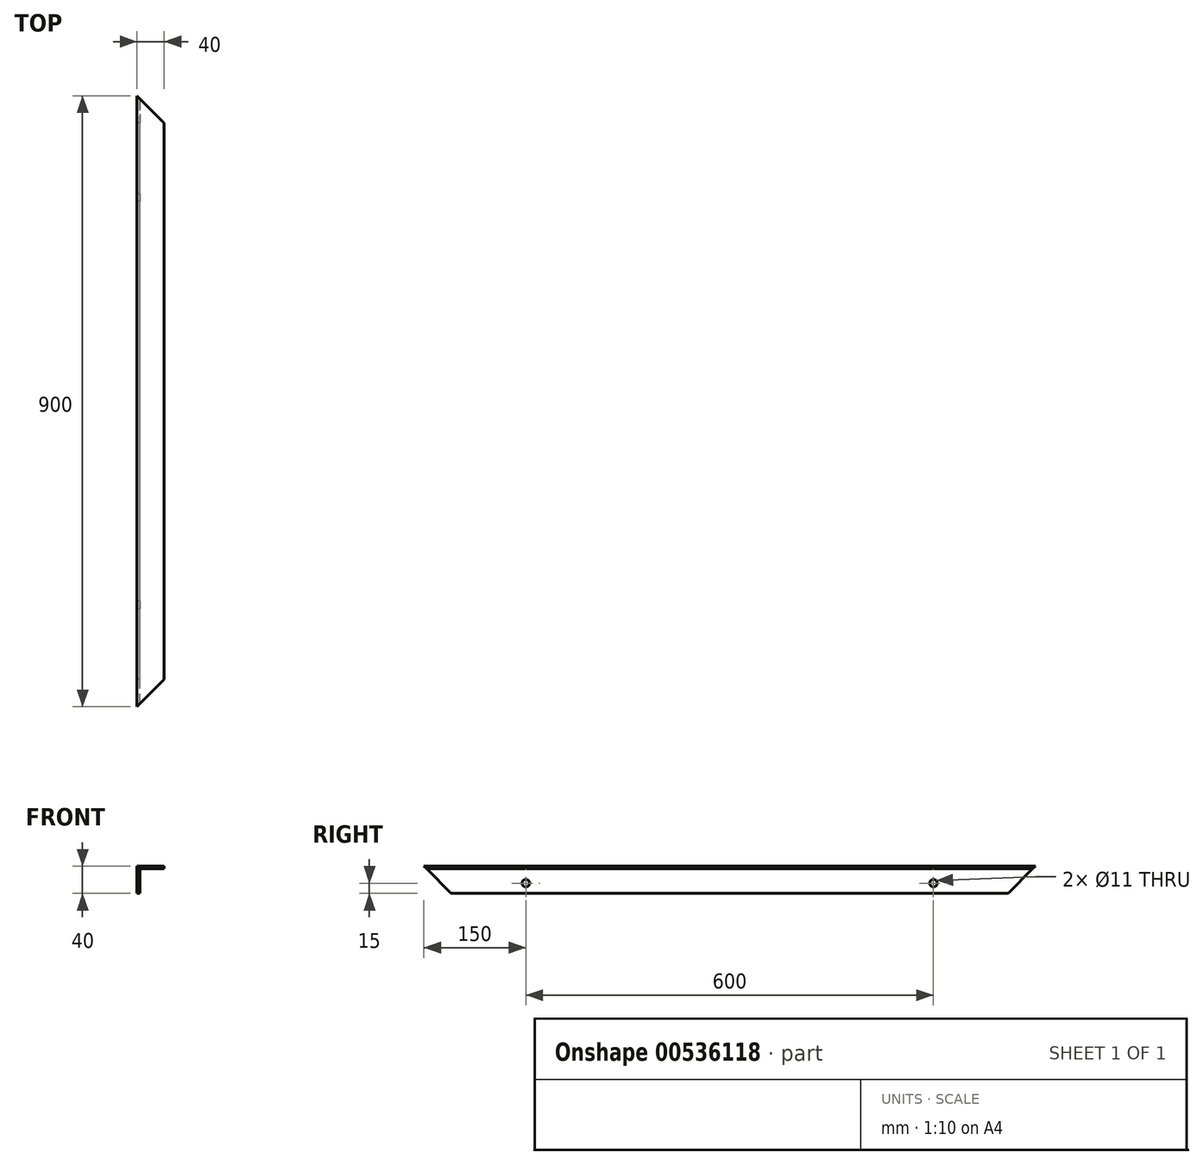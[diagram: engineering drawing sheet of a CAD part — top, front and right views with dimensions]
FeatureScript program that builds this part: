
annotation { "Feature Type Name" : "Feature", "Feature Type Description" : "" }
export const myFeature = defineFeature(function(context is Context, id is Id, definition is map)
    precondition{}
    {
        {
            var Q0;
            Q0=qCreatedBy(makeId("Front.planeOp"),FACE);
            var sketch = newSketch(context, id + "F0", { "sketchPlane" : qUnion([Q0])});
            skLineSegment(sketch, "E0", {"start": v(0, 0) * mm, "end": v(0, 40) * mm});
            skLineSegment(sketch, "E1", {"start": v(0, 40) * mm, "end": v(40, 40) * mm});
            skLineSegment(sketch, "E2.0", {"start": v(4, 36) * mm, "end": v(40, 36) * mm});
            skLineSegment(sketch, "E2.1", {"start": v(4, 0) * mm, "end": v(4, 36) * mm});
            skLineSegment(sketch, "E3", {"start": v(0, 0) * mm, "end": v(4, 0) * mm});
            skLineSegment(sketch, "E4", {"start": v(40, 36) * mm, "end": v(40, 40) * mm});
            skSolve(sketch);
        }
        {
            var Q0;
            Q0=makeQuery(id+"F0.imprint","IMPRINT",FACE,{"disambiguationData":[TD([[makeQuery(id+"F0.imprint","IMPRINT",EDGE,{"derivedFrom":sQuery(id+"F0.wireOp",EDGE,"E0")}),-1.0]])]});
            extrude(context, id + "F1", {"entities" : qUnion([Q0]), "endBound" : BoundingType.SYMMETRIC, "depth" : 900 * mm, "offsetDistance" : 25 * mm});
        }
        {
            var Q0;
            Q0=makeQuery(id+"F1.opExtrude","SWEPT_FACE",FACE,{"disambiguationData":[OSD([sQuery(id+"F0.wireOp",EDGE,"E0")])]});
            var sketch = newSketch(context, id + "F2", { "sketchPlane" : qUnion([Q0])});
            skLineSegment(sketch, "E5", {"start": v(-450, 40) * mm, "end": v(-410, 0) * mm});
            skLineSegment(sketch, "E6", {"start": v(450, 40) * mm, "end": v(410, 0) * mm});
            skSolve(sketch);
        }
        {
            var Q0;
            {var subQ0=sQuery(id+"F2.wireOp",EDGE,"E5");Q0=makeQuery(id+"F2.imprint","IMPRINT",FACE,{"disambiguationData":[TD([[makeQuery(id+"F2.imprint","IMPRINT",EDGE,{"derivedFrom":subQ0}),-1.0]])]});}
            var Q1;
            {var subQ0=sQuery(id+"F2.wireOp",EDGE,"E6");Q1=makeQuery(id+"F2.imprint","IMPRINT",FACE,{"disambiguationData":[TD([[makeQuery(id+"F2.imprint","IMPRINT",EDGE,{"derivedFrom":subQ0}),1.0]])]});}
            extrude(context, id + "F3", {"entities" : qUnion([Q0, Q1]), "operationType" : NewBodyOperationType.REMOVE, "oppositeDirection" : true, "depth" : 40 * mm, "offsetDistance" : 25 * mm});
        }
        {
            var Q0;
            Q0=makeQuery(id+"F1.opExtrude","SWEPT_FACE",FACE,{"disambiguationData":[OSD([sQuery(id+"F0.wireOp",EDGE,"E1")])]});
            var sketch = newSketch(context, id + "F4", { "sketchPlane" : qUnion([Q0])});
            skLineSegment(sketch, "E7", {"start": v(0, 450) * mm, "end": v(40, 410) * mm});
            skLineSegment(sketch, "E8", {"start": v(0, -450) * mm, "end": v(40, -410) * mm});
            skSolve(sketch);
        }
        {
            var Q0;
            {var subQ0=sQuery(id+"F4.wireOp",EDGE,"E7");Q0=makeQuery(id+"F4.imprint","IMPRINT",FACE,{"disambiguationData":[TD([[makeQuery(id+"F4.imprint","IMPRINT",EDGE,{"derivedFrom":subQ0}),1.0]])]});}
            var Q1;
            {var subQ0=sQuery(id+"F4.wireOp",EDGE,"E8");Q1=makeQuery(id+"F4.imprint","IMPRINT",FACE,{"disambiguationData":[TD([[makeQuery(id+"F4.imprint","IMPRINT",EDGE,{"derivedFrom":subQ0}),-1.0]])]});}
            extrude(context, id + "F5", {"entities" : qUnion([Q0, Q1]), "operationType" : NewBodyOperationType.REMOVE, "oppositeDirection" : true, "depth" : 40 * mm, "offsetDistance" : 25 * mm});
        }
        {
            var Q0;
            Q0=makeQuery(id+"F1.opExtrude","SWEPT_FACE",FACE,{"disambiguationData":[OSD([sQuery(id+"F0.wireOp",EDGE,"E0")])]});
            var sketch = newSketch(context, id + "F6", { "sketchPlane" : qUnion([Q0])});
            skLineSegment(sketch, "E9", {"start": v(450, 40) * mm, "end": v(300, 40) * mm});
            skLineSegment(sketch, "E10", {"start": v(300, 40) * mm, "end": v(300, 15) * mm});
            skLineSegment(sketch, "E11", {"start": v(-450, 40) * mm, "end": v(-300, 40) * mm});
            skLineSegment(sketch, "E12", {"start": v(-300, 40) * mm, "end": v(-300, 15) * mm});
            skSolve(sketch);
        }
        {
            var Q0;
            Q0=sQuery(id+"F6.wireOp",VERTEX,"E10.end");
            var Q1;
            Q1=sQuery(id+"F6.wireOp",VERTEX,"E12.end");
            var Q2;
            Q2=makeQuery(id+"F1.opExtrude","SWEPT_BODY",BODY,{"disambiguationData":[OSD([sQuery(id+"F0.wireOp",EDGE,"E0"),sQuery(id+"F0.wireOp",EDGE,"E1"),sQuery(id+"F0.wireOp",EDGE,"E2.0"),sQuery(id+"F0.wireOp",EDGE,"E2.1"),sQuery(id+"F0.wireOp",EDGE,"E3"),sQuery(id+"F0.wireOp",EDGE,"E4")])]});
            hole(context, id + "F7", {"style" : HoleStyle.SIMPLE, "endStyle" : HoleEndStyle.THROUGH, "standardTappedOrClearance" : lookupTablePath({ "standard" : "ISO", "fit" : "Normal", "size" : "M10", "type" : "Clearance" }), "standardBlindInLast" : lookupTablePath({ "fit" : "Standard", "standard" : "ISO", "size" : "M10", "type" : "Clearance" }), "holeDiameter" : 11 * mm, "isTappedThrough" : true, "tappedDepth" : 12 * mm, "tapClearance" : 3, "locations" : qUnion([Q0, Q1]), "scope" : qUnion([Q2])});
        }
    });
